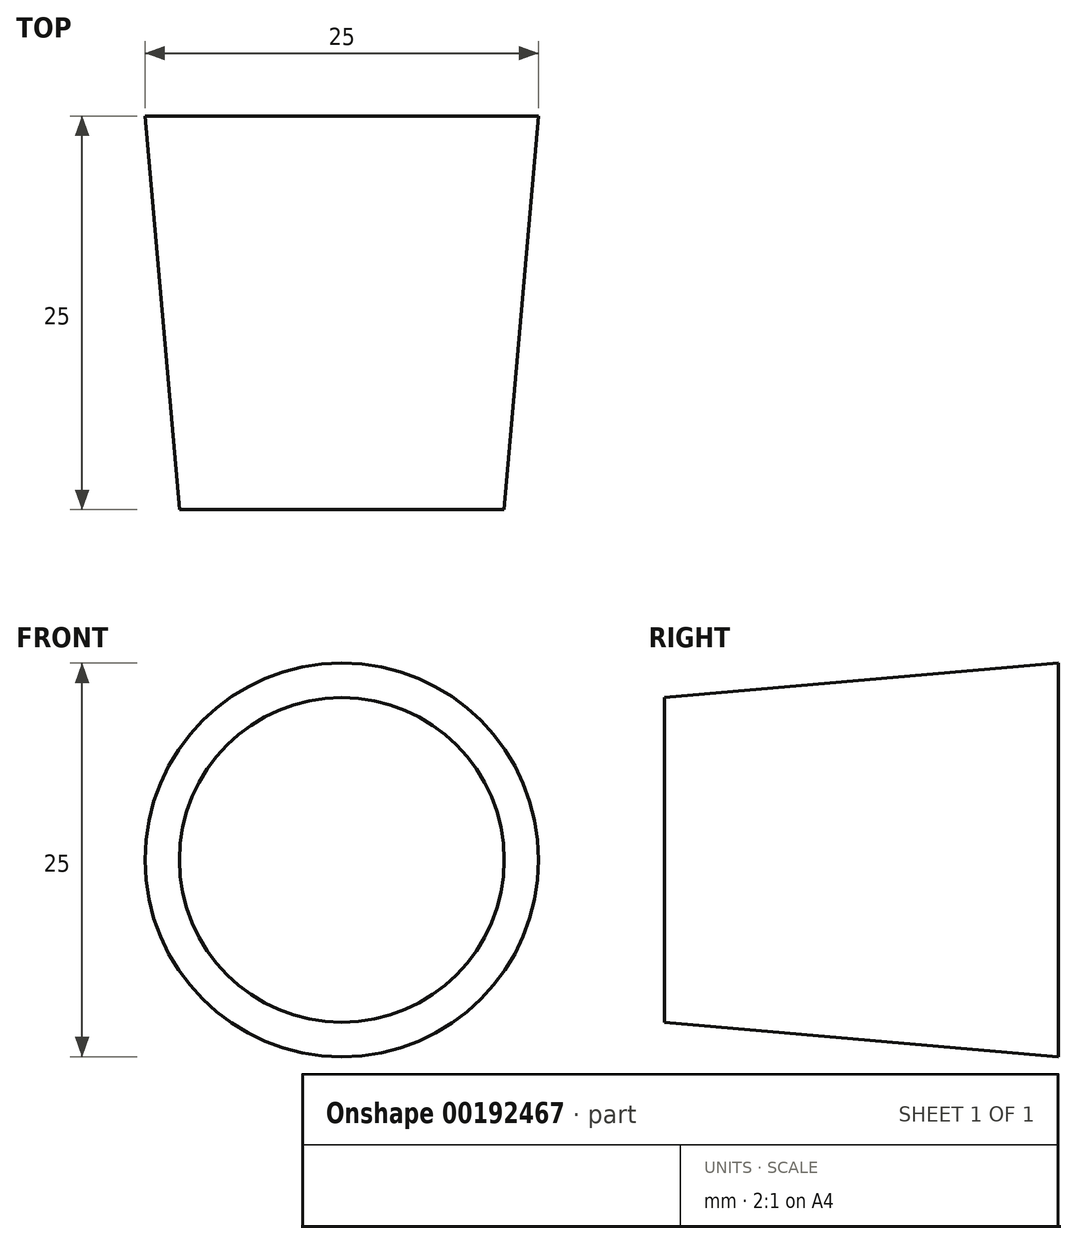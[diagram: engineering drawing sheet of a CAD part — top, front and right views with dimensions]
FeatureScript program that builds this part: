
annotation { "Feature Type Name" : "Feature", "Feature Type Description" : "" }
export const myFeature = defineFeature(function(context is Context, id is Id, definition is map)
    precondition{}
    {
        {
            var Q0;
            Q0=qCreatedBy(makeId("Front.planeOp"),FACE);
            var sketch = newSketch(context, id + "F0", { "sketchPlane" : qUnion([Q0])});
            skCircle(sketch, "E0", {"center": v(0, 0) * mm, "radius": 12.5 * mm});
            skSolve(sketch);
        }
        {
            var Q0;
            Q0 = qSketchRegion(id + "F0", true);
            extrude(context, id + "F1", {"entities" : qUnion([Q0]), "depth" : 25 * mm, "hasDraft" : true, "draftAngle" : 5 * degree, "draftPullDirection" : true});
        }
    });
